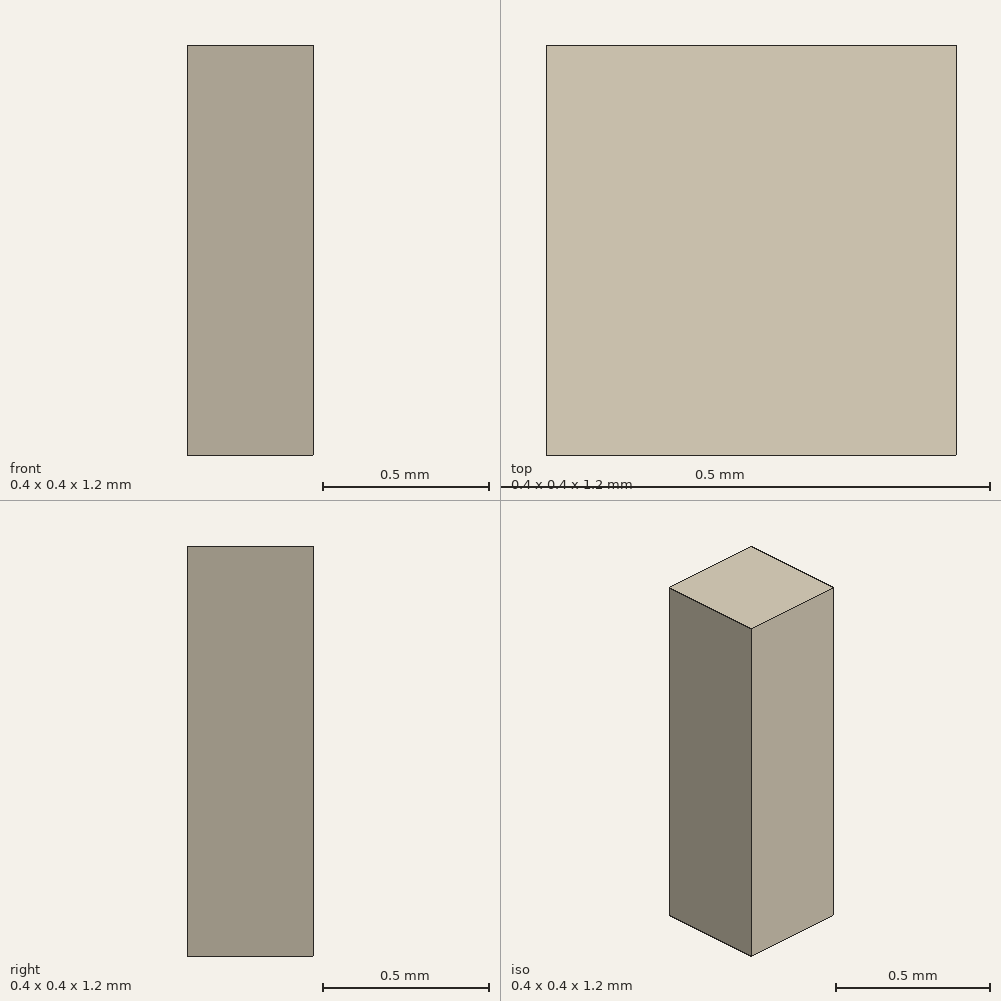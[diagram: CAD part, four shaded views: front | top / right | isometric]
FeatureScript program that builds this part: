
annotation { "Feature Type Name" : "Feature", "Feature Type Description" : "" }
export const myFeature = defineFeature(function(context is Context, id is Id, definition is map)
    precondition{}
    {
        {
            var Q0;
            Q0=qCreatedBy(makeId("Front.planeOp"),FACE);
            var sketch = newSketch(context, id + "F0", { "sketchPlane" : qUnion([Q0])});
            skLineSegment(sketch, "E0.bottom", {"start": v(-0.2, 0.62) * mm, "end": v(0.2, 0.62) * mm});
            skLineSegment(sketch, "E0.top", {"start": v(-0.2, -0.62) * mm, "end": v(0.2, -0.62) * mm});
            skLineSegment(sketch, "E0.left", {"start": v(-0.2, 0.62) * mm, "end": v(-0.2, -0.62) * mm});
            skLineSegment(sketch, "E0.right", {"start": v(0.2, 0.62) * mm, "end": v(0.2, -0.62) * mm});
            skPoint(sketch, "E0.middle", {"position": v(0, 0) * mm});
            skSolve(sketch);
        }
        {
            var Q0;
            Q0=makeQuery(id+"F0.imprint","IMPRINT",FACE,{"disambiguationData":[TD([[makeQuery(id+"F0.imprint","IMPRINT",EDGE,{"derivedFrom":sQuery(id+"F0.wireOp",EDGE,"E0.bottom")}),-1.0]])]});
            extrude(context, id + "F1", {"entities" : qUnion([Q0]), "oppositeDirection" : true, "depth" : 0.38 * mm, "offsetDistance" : 25.4 * mm});
        }
    });
